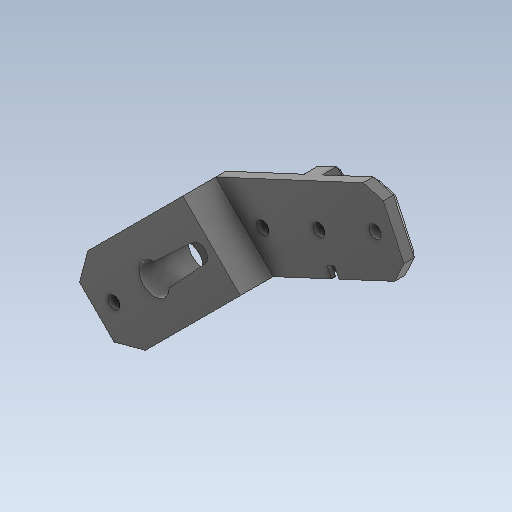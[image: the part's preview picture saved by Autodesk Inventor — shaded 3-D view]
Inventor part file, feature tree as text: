
AUTODESK INVENTOR PART (.ipt)
format: ipt  version: 2020 (Build 240168000, 168)  size: 371,200 bytes
history: native  units: in
note: dims shown in document units (in); Inventor stores cm internally (conversion verified against a paired STEP export)
features: sketch x11, other x6, extrude x5, projected_geometry x3, reference x1
ambient origin geometry x8: Origin, YZ Plane, XZ Plane, XY Plane, X Axis, Y Axis, Z Axis, Center Point
bodies: Solid1 (feature_tree)
feature tree (26):
  other  "TibiaTop.ipt"
  extrude  "Extrusion1"  Depth=0.3937in TaperAngle=0.0deg
  extrude  "Extrusion2"  Depth=0.1969in
  extrude  "Extrusion3"  Depth=0.0398in
  extrude  "Extrusion8"  Depth=0.1575in
  extrude  "Extrusion9"  Depth=0.4761in
  other  "Solid2::TibiaTop.ipt"
  other  "TaggingFeature1"
  sketch  "Sketch1"  dims[d0=0.3937in d1=0.3937in d2=0.0in]
  sketch  "Sketch9"  dims[d5=0.0398in d6=0.0398in]
  sketch  "Sketch10"  dims[d8=0.6142in d9=0.1575in]
  sketch  "Sketch11"  dims[d10=0.4761in d11=0.4761in]
  sketch  "Sketch15"  dims[d14=0.0059in]
  sketch  "Sketch25"  dims[d17=0.3307in d18=0.0in]
  sketch  "Sketch26"  dims[d33=0.2756in d34=0.0787in d35=0.0in d36=0.2756in d37=0.0787in d38=0.0in d24=0.0197in d25=0.0344in d26=0.0197in d27=0.0344in]
  sketch  "Sketch8"  dims[d3=0.2835in d4=0.1969in]
  sketch  "Sketch12"  dims[d12=0.0059in]
  reference  "Reference1"
  sketch  "Sketch13"  dims[d13=0.0059in]
  projected_geometry  "Projected Loop1"
  projected_geometry  "Projected Loop6"
  sketch  "Sketch20"  dims[d15=0.3307in d16=0.0in]
  projected_geometry  "Projected Loop7"
  parser-record x1  (decoder bookkeeping rows leaked as tree rows — omitted from the tree; the rows remain in map.json)
  other  "LegDemoRight.iam"
  other  "TibiaTop:1"
note: 1 file-system path scrubbed to <path> (originals preserved in map.json)
